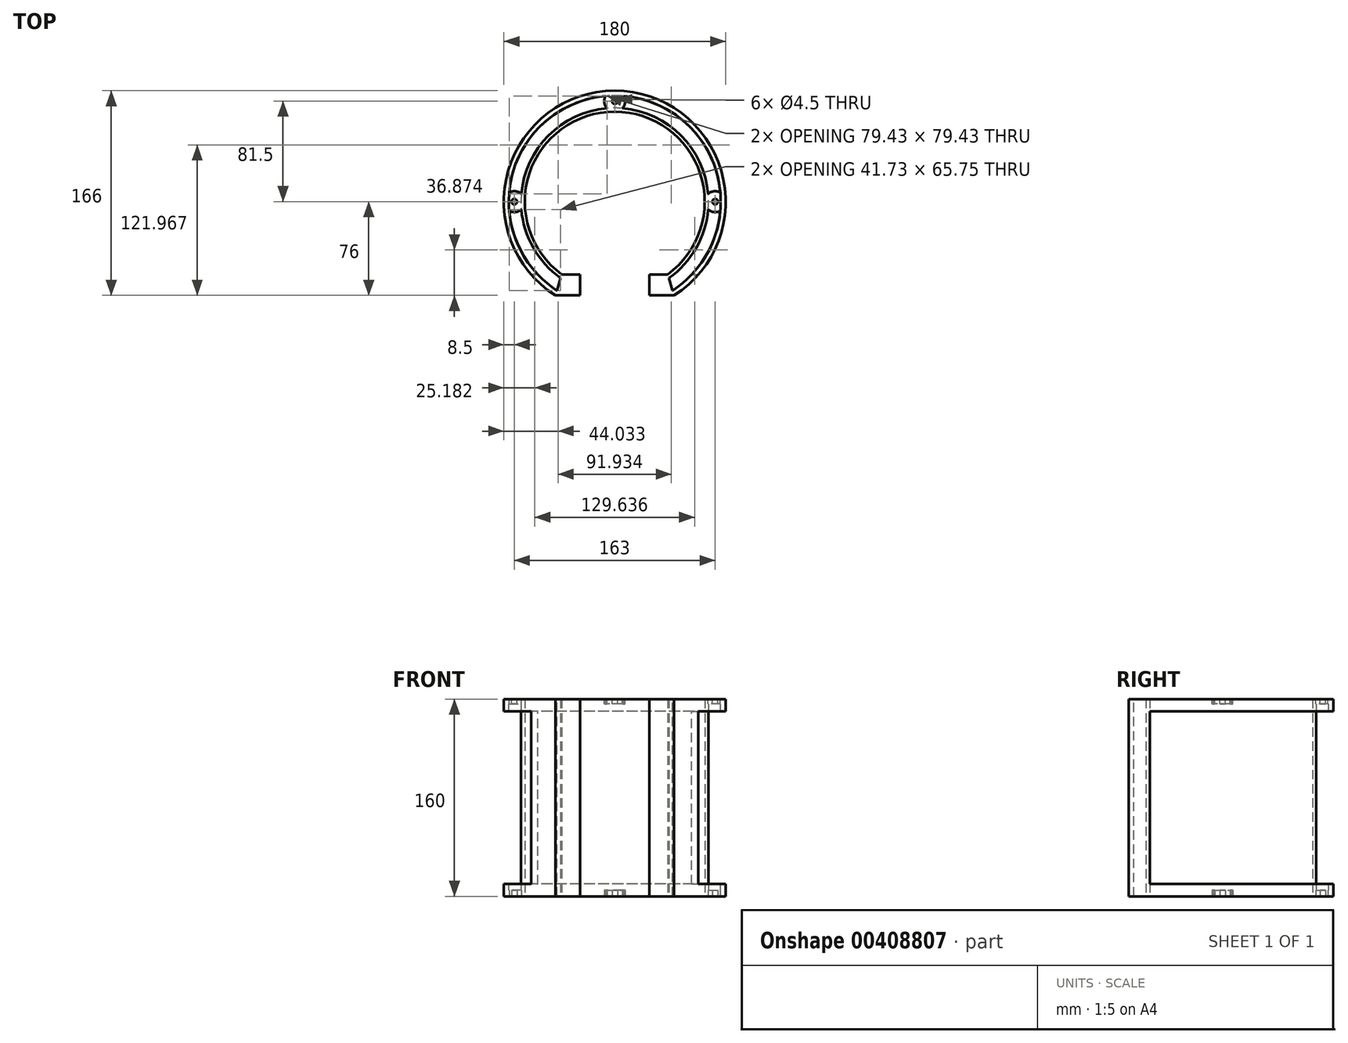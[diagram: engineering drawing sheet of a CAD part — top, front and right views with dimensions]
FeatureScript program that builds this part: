
annotation { "Feature Type Name" : "Feature", "Feature Type Description" : "" }
export const myFeature = defineFeature(function(context is Context, id is Id, definition is map)
    precondition{}
    {
        {
            var Q0;
            Q0=qCreatedBy(makeId("Top.planeOp"),FACE);
            var sketch = newSketch(context, id + "F0", { "sketchPlane" : qUnion([Q0])});
            skArc(sketch, "E0", {"start": v(48.2, -76) * mm, "mid": v(0, 90) * mm, "end": v(-48.2, -76) * mm});
            skLineSegment(sketch, "E1", {"start": v(-48.2, -76) * mm, "end": v(48.2, -76) * mm});
            skCircle(sketch, "E2", {"center": v(0, 0) * mm, "radius": 45 * mm, "construction": true});
            skSolve(sketch);
        }
        {
            var Q0;
            Q0=makeQuery(id+"F0.imprint","IMPRINT",FACE,{"disambiguationData":[TD([[makeQuery(id+"F0.imprint","IMPRINT",EDGE,{"derivedFrom":sQuery(id+"F0.wireOp",EDGE,"E0")}),1.0]])]});
            extrude(context, id + "F1", {"entities" : qUnion([Q0]), "depth" : 160 * mm});
        }
        {
            var Q0;
            Q0=makeQuery(id+"F1.opExtrude","CAP_FACE",FACE,{"disambiguationData":[OSD([sQuery(id+"F0.wireOp",EDGE,"E0"),sQuery(id+"F0.wireOp",EDGE,"E1")])],"isStart":false});
            var sketch = newSketch(context, id + "F2", { "sketchPlane" : qUnion([Q0])});
            skArc(sketch, "E3.0", {"start": v(47.03, -72) * mm, "mid": v(0, 86) * mm, "end": v(-47.03, -72) * mm});
            skLineSegment(sketch, "E3.1", {"start": v(-47.03, -72) * mm, "end": v(47.03, -72) * mm});
            skSolve(sketch);
        }
        {
            var Q0;
            Q0=makeQuery(id+"F2.imprint","IMPRINT",FACE,{"disambiguationData":[TD([[makeQuery(id+"F2.imprint","IMPRINT",EDGE,{"derivedFrom":sQuery(id+"F2.wireOp",EDGE,"E3.0")}),1.0]])]});
            extrude(context, id + "F3", {"entities" : qUnion([Q0]), "operationType" : NewBodyOperationType.REMOVE, "endBound" : BoundingType.UP_TO_NEXT, "oppositeDirection" : true, "depth" : 154 * mm});
        }
        {
            var Q0;
            Q0=makeQuery(id+"F1.opExtrude","SWEPT_FACE",FACE,{"disambiguationData":[OSD([sQuery(id+"F0.wireOp",EDGE,"E1")])]});
            var sketch = newSketch(context, id + "F4", { "sketchPlane" : qUnion([Q0])});
            skLineSegment(sketch, "E4.0", {"start": v(-28.2, 160) * mm, "end": v(-28.2, 0) * mm});
            skLineSegment(sketch, "E5.0", {"start": v(28.2, 160) * mm, "end": v(28.2, 0) * mm});
            skSolve(sketch);
        }
        {
            var Q0;
            Q0=qSketchRegion(id+"F4",true);
            var Q1;
            {var subQ0=sQuery(id+"F4.wireOp",EDGE,"E4.0");Q1=makeQuery(id+"F4.imprint","IMPRINT",FACE,{"disambiguationData":[TD([[makeQuery(id+"F4.imprint","IMPRINT",EDGE,{"derivedFrom":subQ0}),1.0]])]});}
            extrude(context, id + "F5", {"entities" : qUnion([Q0, Q1]), "operationType" : NewBodyOperationType.REMOVE, "endBound" : BoundingType.UP_TO_NEXT, "oppositeDirection" : true, "depth" : 25 * mm});
        }
        {
            var Q0;
            Q0=qCreatedBy(makeId("Top.planeOp"),FACE);
            var sketch = newSketch(context, id + "F6", { "sketchPlane" : qUnion([Q0])});
            skLineSegment(sketch, "E6.0", {"start": v(-43.95, -62) * mm, "end": v(-28.2, -62) * mm});
            skArc(sketch, "E6.1", {"start": v(43.95, -62) * mm, "mid": v(0, 76) * mm, "end": v(-43.95, -62) * mm});
            skLineSegment(sketch, "E6.2", {"start": v(28.2, -62) * mm, "end": v(43.95, -62) * mm});
            skLineSegment(sketch, "E7", {"start": v(-43.95, -62) * mm, "end": v(-46.92, -72.02) * mm});
            skLineSegment(sketch, "E8", {"start": v(-46.92, -72.02) * mm, "end": v(-28.15, -72.02) * mm});
            skLineSegment(sketch, "E9.MirrorCS", {"start": v(43.95, -62) * mm, "end": v(46.92, -72.02) * mm});
            skLineSegment(sketch, "E10.MirrorCS", {"start": v(46.92, -72.02) * mm, "end": v(28.15, -72.02) * mm});
            skArc(sketch, "E11.0", {"start": v(42.22, -59.55) * mm, "mid": v(0, 73) * mm, "end": v(-42.22, -59.55) * mm});
            skLineSegment(sketch, "E12.0", {"start": v(-43.95, -59) * mm, "end": v(-28.2, -59) * mm});
            skLineSegment(sketch, "E13.0", {"start": v(28.2, -59) * mm, "end": v(43.95, -59) * mm});
            skLineSegment(sketch, "E14", {"start": v(-28.2, -59) * mm, "end": v(-28.2, -75.99) * mm});
            skLineSegment(sketch, "E15", {"start": v(28.2, -59) * mm, "end": v(28.2, -75.87) * mm});
            skSolve(sketch);
        }
        {
            var Q0;
            Q0 = qSketchRegion(id + "F6", true);
            extrude(context, id + "F7", {"entities" : qUnion([Q0]), "operationType" : NewBodyOperationType.ADD, "depth" : 160 * mm});
        }
        {
            var Q0;
            Q0=makeQuery(id+"F1.opExtrude","SWEPT_BODY",BODY,{"disambiguationData":[OSD([sQuery(id+"F0.wireOp",EDGE,"E0"),sQuery(id+"F0.wireOp",EDGE,"E1")])]});
            transform(context, id + "F8", {"entities" : qUnion([Q0]), "transformType" : TransformType.TRANSLATION_3D, "dx" : 0 * mm, "dy" : 0 * mm, "dz" : -80 * mm, "makeCopy" : false});
        }
        {
            var Q0;
            Q0=qCreatedBy(makeId("Top.planeOp"),FACE);
            var sketch = newSketch(context, id + "F9", { "sketchPlane" : qUnion([Q0])});
            skArc(sketch, "E16.0", {"start": v(48.2, -76) * mm, "mid": v(0, 90) * mm, "end": v(-48.2, -76) * mm});
            skArc(sketch, "E17.0", {"start": v(47.03, -72) * mm, "mid": v(0, 86) * mm, "end": v(-47.03, -72) * mm});
            skLineSegment(sketch, "E18", {"start": v(-62.53, -59.04) * mm, "end": v(-67.93, -59.04) * mm});
            skLineSegment(sketch, "E19", {"start": v(62.5, -59.08) * mm, "end": v(67.9, -59.08) * mm});
            skSolve(sketch);
        }
        {
            var Q0;
            Q0 = qSketchRegion(id + "F9", true);
            extrude(context, id + "F10", {"entities" : qUnion([Q0]), "operationType" : NewBodyOperationType.REMOVE, "endBound" : BoundingType.SYMMETRIC, "oppositeDirection" : true, "depth" : 140 * mm});
        }
        {
            var Q0;
            Q0=makeQuery(id+"F7.boolean.opBoolean","MERGE",FACE,{"derivedFrom":[makeQuery(id+"F1.opExtrude","CAP_FACE",FACE,{"disambiguationData":[OSD([sQuery(id+"F0.wireOp",EDGE,"E0"),sQuery(id+"F0.wireOp",EDGE,"E1")])],"isStart":false}),makeQuery(id+"F7.opExtrude","CAP_FACE",FACE,{"disambiguationData":[OSD([sQuery(id+"F6.wireOp",EDGE,"E6.1"),sQuery(id+"F6.wireOp",EDGE,"E7"),sQuery(id+"F6.wireOp",EDGE,"E8"),sQuery(id+"F6.wireOp",EDGE,"E9.MirrorCS"),sQuery(id+"F6.wireOp",EDGE,"E10.MirrorCS"),sQuery(id+"F6.wireOp",EDGE,"E11.0"),sQuery(id+"F6.wireOp",EDGE,"E12.0"),sQuery(id+"F6.wireOp",EDGE,"E13.0"),sQuery(id+"F6.wireOp",EDGE,"E14"),sQuery(id+"F6.wireOp",EDGE,"E15")])],"isStart":false})]});
            var sketch = newSketch(context, id + "F11", { "sketchPlane" : qUnion([Q0])});
            skCircle(sketch, "E20", {"center": v(0, 81.5) * mm, "radius": 8.5 * mm});
            skCircle(sketch, "E21", {"center": v(0, 81.5) * mm, "radius": 2.25 * mm});
            skCircle(sketch, "E22.1.0", {"center": v(-81.5, 0) * mm, "radius": 8.5 * mm});
            skCircle(sketch, "E22.2.0", {"center": v(0, -81.5) * mm, "radius": 8.5 * mm});
            skCircle(sketch, "E22.3.0", {"center": v(81.5, 0) * mm, "radius": 8.5 * mm});
            skPoint(sketch, "E22.center", {"position": v(0, 0) * mm});
            skCircle(sketch, "E23.1.0", {"center": v(-81.5, 0) * mm, "radius": 2.25 * mm});
            skCircle(sketch, "E23.2.0", {"center": v(0, -81.5) * mm, "radius": 2.25 * mm});
            skCircle(sketch, "E23.3.0", {"center": v(81.5, 0) * mm, "radius": 2.25 * mm});
            skSolve(sketch);
        }
        {
            var Q0;
            Q0=makeQuery(id+"F11.imprint","IMPRINT",FACE,{"disambiguationData":[TD([[makeQuery(id+"F11.imprint","IMPRINT",EDGE,{"derivedFrom":sQuery(id+"F11.wireOp",EDGE,"E23.1.0")}),-1.0]])]});
            var Q1;
            Q1=makeQuery(id+"F11.imprint","IMPRINT",FACE,{"disambiguationData":[TD([[makeQuery(id+"F11.imprint","IMPRINT",EDGE,{"derivedFrom":sQuery(id+"F11.wireOp",EDGE,"E21")}),-1.0]])]});
            var Q2;
            Q2=makeQuery(id+"F11.imprint","IMPRINT",FACE,{"disambiguationData":[TD([[makeQuery(id+"F11.imprint","IMPRINT",EDGE,{"derivedFrom":sQuery(id+"F11.wireOp",EDGE,"E23.3.0")}),-1.0]])]});
            var Q3;
            {var subQ0=sQuery(id+"F11.wireOp",EDGE,"E22.3.0");var subQ1=makeQuery(id+"F11.imprint","INTERSECT",VERTEX,{"derivedFrom":[makeQuery(id+"F1.opExtrude","CAP_EDGE",EDGE,{"disambiguationData":[OSD([sQuery(id+"F0.wireOp",EDGE,"E0")])],"isStart":false}),subQ0]});Q3=makeQuery(id+"F11.imprint","IMPRINT",FACE,{"disambiguationData":[TD([[makeQuery(id+"F11.imprint","IMPRINT",EDGE,{"disambiguationData":[TD([[subQ1,1.0]])],"derivedFrom":subQ0}),1.0]])]});}
            var Q4;
            {var subQ0=sQuery(id+"F11.wireOp",EDGE,"E20");var subQ1=makeQuery(id+"F11.imprint","INTERSECT",VERTEX,{"derivedFrom":[makeQuery(id+"F1.opExtrude","CAP_EDGE",EDGE,{"disambiguationData":[OSD([sQuery(id+"F0.wireOp",EDGE,"E0")])],"isStart":false}),subQ0]});Q4=makeQuery(id+"F11.imprint","IMPRINT",FACE,{"disambiguationData":[TD([[makeQuery(id+"F11.imprint","IMPRINT",EDGE,{"disambiguationData":[TD([[subQ1,1.0]])],"derivedFrom":subQ0}),1.0]])]});}
            var Q5;
            {var subQ0=sQuery(id+"F11.wireOp",EDGE,"E22.1.0");var subQ1=makeQuery(id+"F11.imprint","INTERSECT",VERTEX,{"derivedFrom":[makeQuery(id+"F1.opExtrude","CAP_EDGE",EDGE,{"disambiguationData":[OSD([sQuery(id+"F0.wireOp",EDGE,"E0")])],"isStart":false}),subQ0]});Q5=makeQuery(id+"F11.imprint","IMPRINT",FACE,{"disambiguationData":[TD([[makeQuery(id+"F11.imprint","IMPRINT",EDGE,{"disambiguationData":[TD([[subQ1,1.0]])],"derivedFrom":subQ0}),1.0]])]});}
            extrude(context, id + "F12", {"entities" : qUnion([Q0, Q1, Q2, Q3, Q4, Q5]), "operationType" : NewBodyOperationType.ADD, "oppositeDirection" : true, "depth" : 4 * mm});
        }
        {
            var Q0;
            Q0=makeQuery(id+"F7.boolean.opBoolean","MERGE",FACE,{"derivedFrom":[makeQuery(id+"F1.opExtrude","CAP_FACE",FACE,{"disambiguationData":[OSD([sQuery(id+"F0.wireOp",EDGE,"E0"),sQuery(id+"F0.wireOp",EDGE,"E1")])],"isStart":true}),makeQuery(id+"F7.opExtrude","CAP_FACE",FACE,{"disambiguationData":[OSD([sQuery(id+"F6.wireOp",EDGE,"E6.1"),sQuery(id+"F6.wireOp",EDGE,"E7"),sQuery(id+"F6.wireOp",EDGE,"E8"),sQuery(id+"F6.wireOp",EDGE,"E9.MirrorCS"),sQuery(id+"F6.wireOp",EDGE,"E10.MirrorCS"),sQuery(id+"F6.wireOp",EDGE,"E11.0"),sQuery(id+"F6.wireOp",EDGE,"E12.0"),sQuery(id+"F6.wireOp",EDGE,"E13.0"),sQuery(id+"F6.wireOp",EDGE,"E14"),sQuery(id+"F6.wireOp",EDGE,"E15")])],"isStart":true})]});
            var sketch = newSketch(context, id + "F13", { "sketchPlane" : qUnion([Q0])});
            skCircle(sketch, "E24", {"center": v(-81.5, 0) * mm, "radius": 8.5 * mm});
            skCircle(sketch, "E25", {"center": v(-81.5, 0) * mm, "radius": 2.25 * mm});
            skCircle(sketch, "E26.1.0", {"center": v(0, -81.5) * mm, "radius": 8.5 * mm});
            skCircle(sketch, "E26.1.1", {"center": v(0, -81.5) * mm, "radius": 2.25 * mm});
            skCircle(sketch, "E26.2.0", {"center": v(81.5, 0) * mm, "radius": 8.5 * mm});
            skCircle(sketch, "E26.2.1", {"center": v(81.5, 0) * mm, "radius": 2.25 * mm});
            skCircle(sketch, "E26.3.0", {"center": v(0, 81.5) * mm, "radius": 8.5 * mm});
            skCircle(sketch, "E26.3.1", {"center": v(0, 81.5) * mm, "radius": 2.25 * mm});
            skPoint(sketch, "E26.center", {"position": v(0, 0) * mm});
            skSolve(sketch);
        }
        {
            var Q0;
            Q0=makeQuery(id+"F13.imprint","IMPRINT",FACE,{"disambiguationData":[TD([[makeQuery(id+"F13.imprint","IMPRINT",EDGE,{"derivedFrom":sQuery(id+"F13.wireOp",EDGE,"E25")}),-1.0]])]});
            var Q1;
            {var subQ0=sQuery(id+"F13.wireOp",EDGE,"E24");var subQ1=sQuery(id+"F0.wireOp",EDGE,"E0");var subQ2=makeQuery(id+"F13.imprint","INTERSECT",VERTEX,{"derivedFrom":[makeQuery(id+"F1.opExtrude","CAP_EDGE",EDGE,{"disambiguationData":[OSD([subQ1])],"isStart":true}),subQ0]});Q1=makeQuery(id+"F13.imprint","IMPRINT",FACE,{"disambiguationData":[TD([[makeQuery(id+"F13.imprint","IMPRINT",EDGE,{"disambiguationData":[TD([[subQ2,1.0]])],"derivedFrom":subQ0}),1.0]])]});}
            var Q2;
            {var subQ0=sQuery(id+"F13.wireOp",EDGE,"E26.2.0");var subQ1=sQuery(id+"F0.wireOp",EDGE,"E0");var subQ2=makeQuery(id+"F13.imprint","INTERSECT",VERTEX,{"derivedFrom":[makeQuery(id+"F1.opExtrude","CAP_EDGE",EDGE,{"disambiguationData":[OSD([subQ1])],"isStart":true}),subQ0]});Q2=makeQuery(id+"F13.imprint","IMPRINT",FACE,{"disambiguationData":[TD([[makeQuery(id+"F13.imprint","IMPRINT",EDGE,{"disambiguationData":[TD([[subQ2,1.0]])],"derivedFrom":subQ0}),1.0]])]});}
            var Q3;
            Q3=makeQuery(id+"F13.imprint","IMPRINT",FACE,{"disambiguationData":[TD([[makeQuery(id+"F13.imprint","IMPRINT",EDGE,{"derivedFrom":sQuery(id+"F13.wireOp",EDGE,"E26.2.1")}),-1.0]])]});
            var Q4;
            Q4=makeQuery(id+"F13.imprint","IMPRINT",FACE,{"disambiguationData":[TD([[makeQuery(id+"F13.imprint","IMPRINT",EDGE,{"derivedFrom":sQuery(id+"F13.wireOp",EDGE,"E26.1.1")}),-1.0]])]});
            var Q5;
            {var subQ0=sQuery(id+"F13.wireOp",EDGE,"E26.1.0");var subQ1=sQuery(id+"F0.wireOp",EDGE,"E0");var subQ2=makeQuery(id+"F13.imprint","INTERSECT",VERTEX,{"derivedFrom":[makeQuery(id+"F1.opExtrude","CAP_EDGE",EDGE,{"disambiguationData":[OSD([subQ1])],"isStart":true}),subQ0]});Q5=makeQuery(id+"F13.imprint","IMPRINT",FACE,{"disambiguationData":[TD([[makeQuery(id+"F13.imprint","IMPRINT",EDGE,{"disambiguationData":[TD([[subQ2,1.0]])],"derivedFrom":subQ0}),1.0]])]});}
            extrude(context, id + "F14", {"entities" : qUnion([Q0, Q1, Q2, Q3, Q4, Q5]), "operationType" : NewBodyOperationType.ADD, "oppositeDirection" : true, "depth" : 5 * mm});
        }
    });
